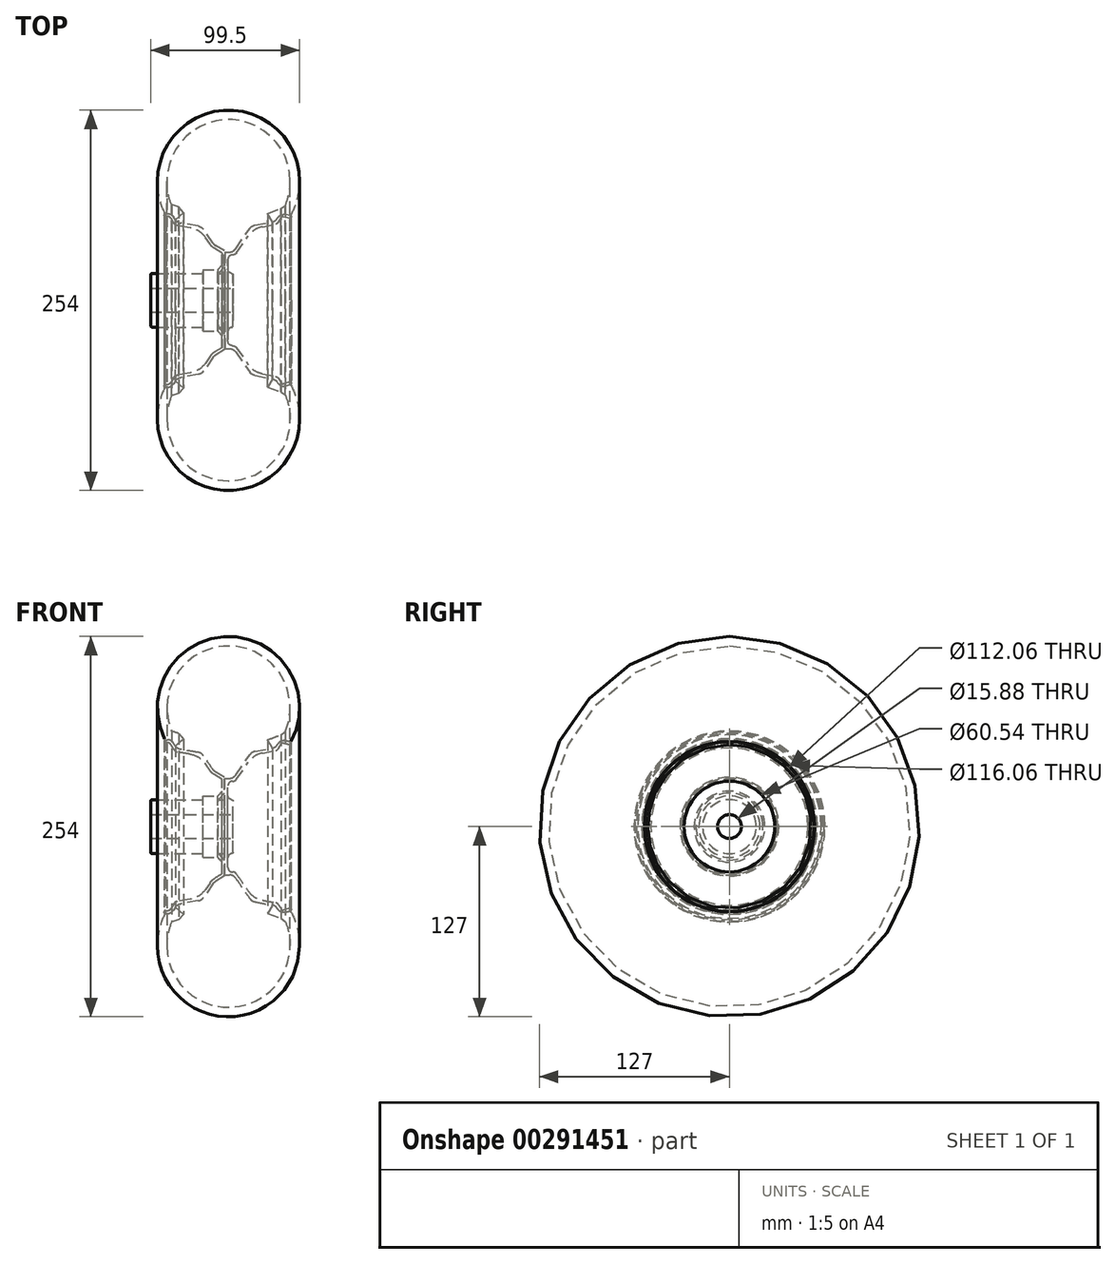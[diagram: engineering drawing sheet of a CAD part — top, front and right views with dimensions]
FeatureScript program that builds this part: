
annotation { "Feature Type Name" : "Feature", "Feature Type Description" : "" }
export const myFeature = defineFeature(function(context is Context, id is Id, definition is map)
    precondition{}
    {
        {
            var Q0;
            Q0=qCreatedBy(makeId("Front.planeOp"),FACE);
            var sketch = newSketch(context, id + "F0", { "sketchPlane" : qUnion([Q0])});
            skLineSegment(sketch, "E0", {"start": v(0, 127) * mm, "end": v(0, -127) * mm, "construction": true});
            skLineSegment(sketch, "E1.bottom", {"start": v(0, 7.94) * mm, "end": v(-55, 7.94) * mm});
            skLineSegment(sketch, "E1.top", {"start": v(0, 17.94) * mm, "end": v(-3.4, 17.94) * mm});
            skLineSegment(sketch, "E1.left", {"start": v(0, 7.94) * mm, "end": v(0, 17.94) * mm});
            skLineSegment(sketch, "E1.right", {"start": v(-55, 7.94) * mm, "end": v(-55, 17.94) * mm});
            skLineSegment(sketch, "E2", {"start": v(177.68, 0) * mm, "end": v(-164.6, 0) * mm, "construction": true});
            skLineSegment(sketch, "E3", {"start": v(-3.4, 17.94) * mm, "end": v(-3.4, 30.27) * mm});
            skLineSegment(sketch, "E4", {"start": v(-3.4, 30.27) * mm, "end": v(1.34, 30.27) * mm});
            skLineSegment(sketch, "E5", {"start": v(1.34, 30.27) * mm, "end": v(13.63, 47.97) * mm});
            skLineSegment(sketch, "E6", {"start": v(13.63, 47.97) * mm, "end": v(29.7, 51.08) * mm});
            skLineSegment(sketch, "E7", {"start": v(29.7, 51.08) * mm, "end": v(32.8, 55.86) * mm});
            skLineSegment(sketch, "E8", {"start": v(31.9, 58.15) * mm, "end": v(39.2, 56.33) * mm});
            skLineSegment(sketch, "E9.0", {"start": v(-5.4, 32.27) * mm, "end": v(0.3, 32.27) * mm});
            skLineSegment(sketch, "E10.0", {"start": v(-5.4, 17.94) * mm, "end": v(-5.4, 32.27) * mm});
            skLineSegment(sketch, "E11.0", {"start": v(12.45, 49.78) * mm, "end": v(28.48, 52.88) * mm});
            skLineSegment(sketch, "E12.0", {"start": v(28.48, 52.88) * mm, "end": v(31.9, 58.15) * mm});
            skLineSegment(sketch, "E13.0", {"start": v(32.8, 55.86) * mm, "end": v(38.7, 54.39) * mm});
            skLineSegment(sketch, "E14.trimOffspring", {"start": v(0.3, 32.27) * mm, "end": v(12.45, 49.78) * mm});
            skLineSegment(sketch, "E15.trimOffspring", {"start": v(-5.4, 17.94) * mm, "end": v(-9.88, 17.94) * mm});
            skLineSegment(sketch, "E16", {"start": v(39.2, 56.33) * mm, "end": v(38.7, 54.39) * mm});
            skLineSegment(sketch, "E17", {"start": v(-20.13, 17.94) * mm, "end": v(-20.13, 20.46) * mm});
            skLineSegment(sketch, "E18", {"start": v(-20.13, 20.46) * mm, "end": v(-10.29, 20.46) * mm});
            skLineSegment(sketch, "E19", {"start": v(-10.29, 20.46) * mm, "end": v(-7.36, 23.68) * mm});
            skLineSegment(sketch, "E20", {"start": v(-7.36, 23.68) * mm, "end": v(-7.36, 31.57) * mm});
            skLineSegment(sketch, "E21", {"start": v(-7.36, 31.57) * mm, "end": v(-14.18, 35.76) * mm});
            skLineSegment(sketch, "E22", {"start": v(-14.18, 35.76) * mm, "end": v(-22.17, 47.36) * mm});
            skLineSegment(sketch, "E23", {"start": v(-22.17, 47.36) * mm, "end": v(-38.54, 50.08) * mm});
            skLineSegment(sketch, "E24", {"start": v(-38.54, 50.08) * mm, "end": v(-42.24, 56.03) * mm});
            skLineSegment(sketch, "E25", {"start": v(-42.24, 56.03) * mm, "end": v(-46.04, 56.03) * mm});
            skLineSegment(sketch, "E26.0", {"start": v(-41.13, 58.03) * mm, "end": v(-46.04, 58.03) * mm});
            skLineSegment(sketch, "E27.0", {"start": v(-37.32, 51.9) * mm, "end": v(-41.13, 58.03) * mm});
            skLineSegment(sketch, "E28.0", {"start": v(-21, 49.19) * mm, "end": v(-37.32, 51.9) * mm});
            skLineSegment(sketch, "E29.0", {"start": v(-12.78, 37.24) * mm, "end": v(-21, 49.19) * mm});
            skLineSegment(sketch, "E30.0", {"start": v(-5.88, 33.01) * mm, "end": v(-12.78, 37.24) * mm});
            skLineSegment(sketch, "E31.0", {"start": v(-9.88, 17.94) * mm, "end": v(-5.88, 22.33) * mm});
            skLineSegment(sketch, "E32", {"start": v(-5.88, 22.33) * mm, "end": v(-5.88, 33.01) * mm});
            skLineSegment(sketch, "E33", {"start": v(-46.04, 58.03) * mm, "end": v(-46.04, 56.03) * mm});
            skLineSegment(sketch, "E34.trimOffspring", {"start": v(-20.13, 17.94) * mm, "end": v(-55, 17.94) * mm});
            skSolve(sketch);
        }
        {
            var Q0;
            Q0=makeQuery(id+"F0.imprint","IMPRINT",FACE,{"disambiguationData":[TD([[makeQuery(id+"F0.imprint","IMPRINT",EDGE,{"derivedFrom":sQuery(id+"F0.wireOp",EDGE,"E1.bottom")}),-1.0]])]});
            var Q1;
            Q1=sQuery(id+"F0.wireOp",EDGE,"E2");
            revolve(context, id + "F1", {"entities" : qUnion([Q0]), "axis" : qUnion([Q1]), "revolveType" : RevolveType.FULL});
        }
        {
            var Q0;
            Q0=makeQuery(id+"F1.opRevolve","SWEPT_EDGE",EDGE,{"disambiguationData":[OSD([sQuery(id+"F0.wireOp",EDGE,"E5"),sQuery(id+"F0.wireOp",EDGE,"E6")])]});
            fillet(context, id + "F2", {"entities" : qUnion([Q0]), "radius" : 15 * mm, "tangentPropagation" : true, "allowEdgeOverflow" : false});
        }
        {
            var Q0;
            Q0=makeQuery(id+"F1.opRevolve","SWEPT_EDGE",EDGE,{"disambiguationData":[OSD([sQuery(id+"F0.wireOp",EDGE,"E3"),sQuery(id+"F0.wireOp",EDGE,"E4")])]});
            var Q1;
            Q1=makeQuery(id+"F1.opRevolve","SWEPT_EDGE",EDGE,{"disambiguationData":[OSD([sQuery(id+"F0.wireOp",EDGE,"E4"),sQuery(id+"F0.wireOp",EDGE,"E5")])]});
            var Q2;
            Q2=makeQuery(id+"F1.opRevolve","SWEPT_EDGE",EDGE,{"disambiguationData":[OSD([sQuery(id+"F0.wireOp",EDGE,"E1.top"),sQuery(id+"F0.wireOp",EDGE,"E3")])]});
            var Q3;
            Q3=makeQuery(id+"F1.opRevolve","SWEPT_EDGE",EDGE,{"disambiguationData":[OSD([sQuery(id+"F0.wireOp",EDGE,"E6"),sQuery(id+"F0.wireOp",EDGE,"E7")])]});
            fillet(context, id + "F3", {"entities" : qUnion([Q0, Q1, Q2, Q3]), "radius" : 3 * mm, "tangentPropagation" : true, "allowEdgeOverflow" : false});
        }
        {
            var Q0;
            Q0=makeQuery(id+"F1.opRevolve","SWEPT_EDGE",EDGE,{"disambiguationData":[OSD([sQuery(id+"F0.wireOp",EDGE,"E7"),sQuery(id+"F0.wireOp",EDGE,"E13.0")])]});
            var Q1;
            Q1=makeQuery(id+"F1.opRevolve","SWEPT_EDGE",EDGE,{"disambiguationData":[OSD([sQuery(id+"F0.wireOp",EDGE,"E13.0"),sQuery(id+"F0.wireOp",EDGE,"E16")])]});
            var Q2;
            Q2=makeQuery(id+"F1.opRevolve","SWEPT_EDGE",EDGE,{"disambiguationData":[OSD([sQuery(id+"F0.wireOp",EDGE,"E8"),sQuery(id+"F0.wireOp",EDGE,"E16")])]});
            fillet(context, id + "F4", {"entities" : qUnion([Q0, Q1, Q2]), "radius" : 1 * mm, "tangentPropagation" : true, "allowEdgeOverflow" : false});
        }
        {
            var Q0;
            Q0=makeQuery(id+"F1.opRevolve","SWEPT_EDGE",EDGE,{"disambiguationData":[OSD([sQuery(id+"F0.wireOp",EDGE,"E11.0"),sQuery(id+"F0.wireOp",EDGE,"E12.0")])]});
            var Q1;
            Q1=makeQuery(id+"F1.opRevolve","SWEPT_EDGE",EDGE,{"disambiguationData":[OSD([sQuery(id+"F0.wireOp",EDGE,"E11.0"),sQuery(id+"F0.wireOp",EDGE,"E14.trimOffspring")])]});
            var Q2;
            Q2=makeQuery(id+"F1.opRevolve","SWEPT_EDGE",EDGE,{"disambiguationData":[OSD([sQuery(id+"F0.wireOp",EDGE,"E8"),sQuery(id+"F0.wireOp",EDGE,"E12.0")])]});
            var Q3;
            Q3=makeQuery(id+"F1.opRevolve","SWEPT_EDGE",EDGE,{"disambiguationData":[OSD([sQuery(id+"F0.wireOp",EDGE,"E27.0"),sQuery(id+"F0.wireOp",EDGE,"E28.0")])]});
            var Q4;
            Q4=makeQuery(id+"F1.opRevolve","SWEPT_EDGE",EDGE,{"disambiguationData":[OSD([sQuery(id+"F0.wireOp",EDGE,"E26.0"),sQuery(id+"F0.wireOp",EDGE,"E27.0")])]});
            var Q5;
            Q5=makeQuery(id+"F1.opRevolve","SWEPT_EDGE",EDGE,{"disambiguationData":[OSD([sQuery(id+"F0.wireOp",EDGE,"E28.0"),sQuery(id+"F0.wireOp",EDGE,"E29.0")])]});
            var Q6;
            Q6=makeQuery(id+"F1.opRevolve","SWEPT_FACE",FACE,{"disambiguationData":[OSD([sQuery(id+"F0.wireOp",EDGE,"E29.0")])]});
            var Q7;
            Q7=makeQuery(id+"F1.opRevolve","SWEPT_EDGE",EDGE,{"disambiguationData":[OSD([sQuery(id+"F0.wireOp",EDGE,"E9.0"),sQuery(id+"F0.wireOp",EDGE,"E14.trimOffspring")])]});
            fillet(context, id + "F5", {"entities" : qUnion([Q0, Q1, Q2, Q3, Q4, Q5, Q6, Q7]), "radius" : 5 * mm, "tangentPropagation" : true, "allowEdgeOverflow" : false});
        }
        {
            var Q0;
            Q0=makeQuery(id+"F1.opRevolve","SWEPT_EDGE",EDGE,{"disambiguationData":[OSD([sQuery(id+"F0.wireOp",EDGE,"E22"),sQuery(id+"F0.wireOp",EDGE,"E23")])]});
            fillet(context, id + "F6", {"entities" : qUnion([Q0]), "radius" : 15 * mm, "tangentPropagation" : true, "allowEdgeOverflow" : false});
        }
        {
            var Q0;
            {var subQ0=sQuery(id+"F0.wireOp",EDGE,"E22");Q0=makeQuery(id+"F6.opFillet","BLEND_EDGE",EDGE,{"blendedFrom":[makeQuery(id+"F1.opRevolve","SWEPT_EDGE",EDGE,{"disambiguationData":[OSD([subQ0,sQuery(id+"F0.wireOp",EDGE,"E23")])]}),makeQuery(id+"F1.opRevolve","SWEPT_FACE",FACE,{"disambiguationData":[OSD([subQ0])]})],"blendedInto":[makeQuery(id+"F1.opRevolve","SWEPT_FACE",FACE,{"disambiguationData":[OSD([subQ0])]})]});}
            var Q1;
            Q1=makeQuery(id+"F1.opRevolve","SWEPT_EDGE",EDGE,{"disambiguationData":[OSD([sQuery(id+"F0.wireOp",EDGE,"E21"),sQuery(id+"F0.wireOp",EDGE,"E22")])]});
            fillet(context, id + "F7", {"entities" : qUnion([Q0, Q1]), "radius" : 10 * mm, "tangentPropagation" : true, "allowEdgeOverflow" : false});
        }
        {
            var Q0;
            Q0=makeQuery(id+"F1.opRevolve","SWEPT_EDGE",EDGE,{"disambiguationData":[OSD([sQuery(id+"F0.wireOp",EDGE,"E23"),sQuery(id+"F0.wireOp",EDGE,"E24")])]});
            var Q1;
            Q1=makeQuery(id+"F1.opRevolve","SWEPT_EDGE",EDGE,{"disambiguationData":[OSD([sQuery(id+"F0.wireOp",EDGE,"E24"),sQuery(id+"F0.wireOp",EDGE,"E25")])]});
            fillet(context, id + "F8", {"entities" : qUnion([Q0, Q1]), "radius" : 3 * mm, "tangentPropagation" : true, "allowEdgeOverflow" : false});
        }
        {
            var Q0;
            Q0=makeQuery(id+"F1.opRevolve","SWEPT_EDGE",EDGE,{"disambiguationData":[OSD([sQuery(id+"F0.wireOp",EDGE,"E26.0"),sQuery(id+"F0.wireOp",EDGE,"E33")])]});
            var Q1;
            Q1=makeQuery(id+"F1.opRevolve","SWEPT_EDGE",EDGE,{"disambiguationData":[OSD([sQuery(id+"F0.wireOp",EDGE,"E25"),sQuery(id+"F0.wireOp",EDGE,"E33")])]});
            fillet(context, id + "F9", {"entities" : qUnion([Q0, Q1]), "radius" : 1 * mm, "tangentPropagation" : true, "allowEdgeOverflow" : false});
        }
        {
            var Q0;
            Q0=makeQuery(id+"F1.opRevolve","SWEPT_EDGE",EDGE,{"disambiguationData":[OSD([sQuery(id+"F0.wireOp",EDGE,"E1.right"),sQuery(id+"F0.wireOp",EDGE,"E34.trimOffspring")])]});
            var Q1;
            Q1=makeQuery(id+"F1.opRevolve","SWEPT_EDGE",EDGE,{"disambiguationData":[OSD([sQuery(id+"F0.wireOp",EDGE,"E1.top"),sQuery(id+"F0.wireOp",EDGE,"E1.left")])]});
            fillet(context, id + "F10", {"entities" : qUnion([Q0, Q1]), "radius" : 1 * mm, "tangentPropagation" : true, "allowEdgeOverflow" : false});
        }
        {
            var Q0;
            Q0=qCreatedBy(makeId("Front.planeOp"),FACE);
            var sketch = newSketch(context, id + "F11", { "sketchPlane" : qUnion([Q0])});
            skArc(sketch, "E35", {"start": v(38.77, 56.88) * mm, "mid": v(-1.98, 126.99) * mm, "end": v(-45.7, 58.69) * mm});
            skLineSegment(sketch, "E36", {"start": v(-8.95, 127) * mm, "end": v(82.11, 127) * mm, "construction": true});
            skArc(sketch, "E37", {"start": v(-45.04, -56.03) * mm, "mid": v(-45.75, -56.32) * mm, "end": v(-46.04, -57.03) * mm});
            skLineSegment(sketch, "E38", {"start": v(-45.04, 58.03) * mm, "end": v(-43.91, 58.03) * mm});
            skArc(sketch, "E39", {"start": v(-39.67, 55.67) * mm, "mid": v(-41.48, 57.4) * mm, "end": v(-43.91, 58.03) * mm});
            skLineSegment(sketch, "E40", {"start": v(-39.67, 55.67) * mm, "end": v(-38.52, 53.83) * mm});
            skLineSegment(sketch, "E41", {"start": v(35.36, 57.28) * mm, "end": v(38.22, 56.57) * mm});
            skArc(sketch, "E42", {"start": v(38.98, -55.6) * mm, "mid": v(38.6, -54.81) * mm, "end": v(37.74, -54.63) * mm});
            skArc(sketch, "E43", {"start": v(35.36, 57.28) * mm, "mid": v(32.32, 57.09) * mm, "end": v(29.95, 55.16) * mm});
            skLineSegment(sketch, "E44", {"start": v(29.63, 54.66) * mm, "end": v(29.95, 55.16) * mm});
            skArc(sketch, "E45", {"start": v(26.4, 52.48) * mm, "mid": v(28.23, 53.24) * mm, "end": v(29.63, 54.66) * mm});
            skLineSegment(sketch, "E46", {"start": v(38.22, 56.57) * mm, "end": v(38.77, 56.88) * mm});
            skLineSegment(sketch, "E47", {"start": v(26.4, 52.48) * mm, "end": v(23.16, 57.98) * mm});
            skLineSegment(sketch, "E48", {"start": v(23.16, 57.98) * mm, "end": v(32.03, 61.3) * mm});
            skLineSegment(sketch, "E49", {"start": v(-38.52, 53.83) * mm, "end": v(-33.05, 58.57) * mm});
            skLineSegment(sketch, "E50", {"start": v(-33.05, 58.57) * mm, "end": v(-36.18, 62.19) * mm});
            skLineSegment(sketch, "E51", {"start": v(-36.18, 62.19) * mm, "end": v(-41.09, 63.8) * mm});
            skLineSegment(sketch, "E52", {"start": v(32.03, 61.3) * mm, "end": v(34.86, 63.25) * mm});
            skArc(sketch, "E53", {"start": v(34.86, 63.25) * mm, "mid": v(-2.7, 120.7) * mm, "end": v(-41.09, 63.8) * mm});
            skLineSegment(sketch, "E54", {"start": v(-45.04, 58.03) * mm, "end": v(-45.7, 58.69) * mm});
            skLineSegment(sketch, "E55", {"start": v(-127.22, 0) * mm, "end": v(107, 0) * mm, "construction": true});
            skSolve(sketch);
        }
        {
            var Q0;
            Q0=makeQuery(id+"F11.imprint","IMPRINT",FACE,{"disambiguationData":[TD([[makeQuery(id+"F11.imprint","IMPRINT",EDGE,{"derivedFrom":sQuery(id+"F11.wireOp",EDGE,"E35")}),1.0]])]});
            var Q1;
            Q1=sQuery(id+"F11.wireOp",EDGE,"E55");
            revolve(context, id + "F12", {"entities" : qUnion([Q0]), "axis" : qUnion([Q1]), "revolveType" : RevolveType.FULL});
        }
    });
